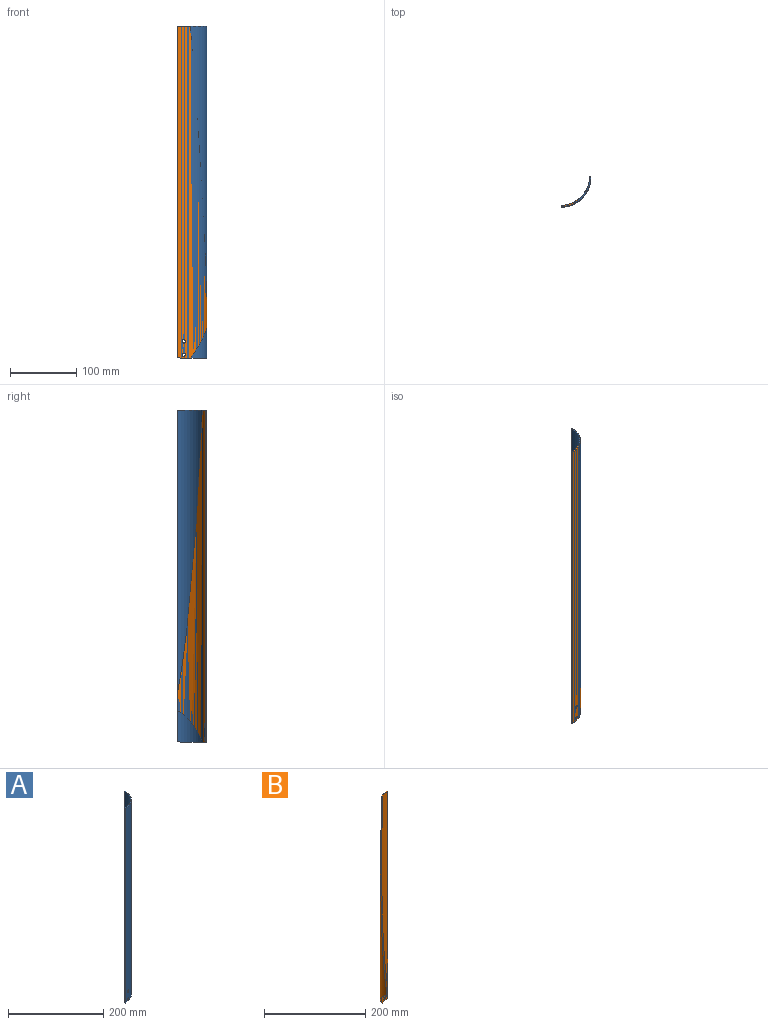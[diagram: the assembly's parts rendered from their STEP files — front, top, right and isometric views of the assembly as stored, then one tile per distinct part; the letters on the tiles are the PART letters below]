
ASSEMBLY  parts=2 mates=1
PART A: 8 faces, bbox 45x45x500 mm
  f0: cylinder r=43mm len=500mm, axis (0,0,-1), area 33731.6mm2, adj f2,f3,f4,f5,f6,f7
  f1: cylinder r=45mm len=500mm, axis (0,0,-1), area 35302.5mm2, adj f2,f3,f4,f5,f6,f7
  f2: plane 45x45mm, normal (0,0,-1), area 138.2mm2, adj f0,f1,f6,f7
  f3: plane 45x45mm, normal (0,0,1), area 138.2mm2, adj f0,f1,f6,f7
  f4: cylinder r=2.5mm len=5mm, axis (0,1,0), area 32.3mm2, adj f0,f1
  f5: cylinder r=2.5mm len=5mm, axis (0,1,0), area 32.3mm2, adj f0,f1
  f6: plane 500x2mm, normal (-1,0,0), area 1000mm2, adj f0,f1,f2,f3
  f7: plane 500x2mm, normal (0,1,0), area 1000mm2, adj f0,f1,f2,f3
PART B: 10 faces, bbox 45x45x500 mm
  f0: cylinder r=43mm len=500mm, axis (0,0,-1), area 20990.6mm2, adj f2,f3,f4,f5,f6,f7,f8,f9
  f1: cylinder r=45mm len=500mm, axis (0,0,-1), area 21348.7mm2, adj f3,f4,f5,f6,f7,f8,f9
  f2: plane 22.22x2mm, normal (0,-1,0), area 22.2mm2, adj f0,f8,f9
  f3: plane 20x6.48mm, normal (0,0,-1), area 40.5mm2, adj f0,f1,f5,f9
  f4: plane 20x6.48mm, normal (0,0,1), area 40.5mm2, adj f0,f1,f5,f8
  f5: plane 500x2mm, normal (1,0,0), area 1000mm2, adj f0,f1,f3,f4
  f6: cylinder r=2.5mm len=5mm, axis (0,-1,0), area 32.3mm2, adj f0,f1
  f7: cylinder r=2.5mm len=5mm, axis (0,-1,0), area 32.3mm2, adj f0,f1
  f8: plane 450x40.31mm, normal (-0.89,-0.44,0.09), area 1095mm2, adj f0,f1,f2,f4
  f9: plane 50x40.31mm, normal (-0.7,-0.35,-0.63), area 155.7mm2, adj f0,f1,f2,f3
PLACE A t=(-59.54,98.01,-104.66)mm
PLACE B rot(axis=(0,0,1),180deg) t=(-59.54,98.01,-104.66)mm
MATE fastened B.f0 <-> A.f0  axis (0,0,-1) through (-59.54,98.01,-104.66)mm
